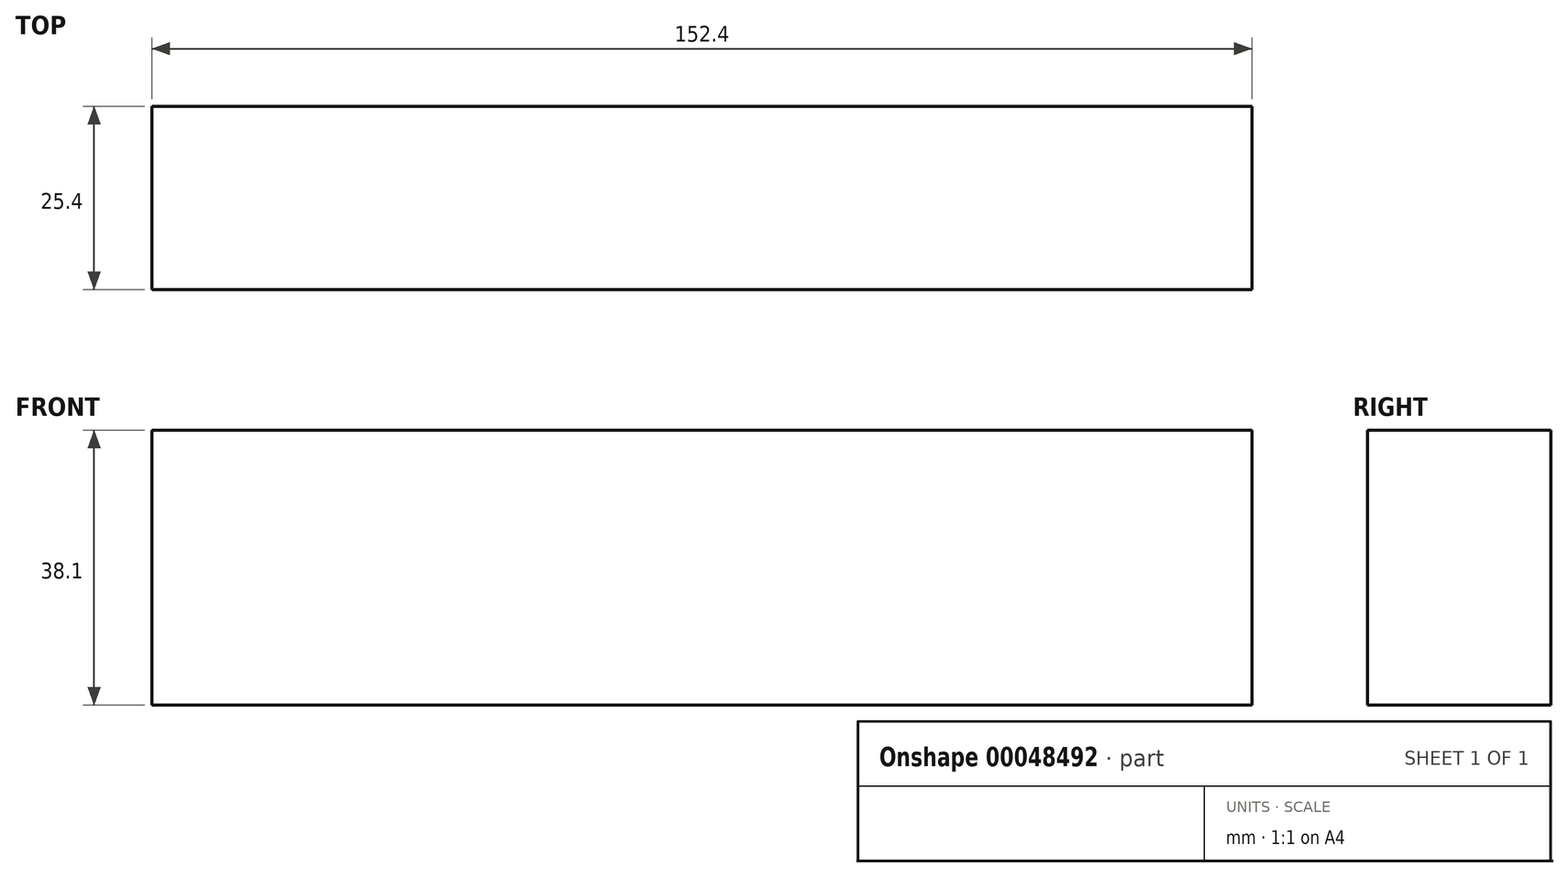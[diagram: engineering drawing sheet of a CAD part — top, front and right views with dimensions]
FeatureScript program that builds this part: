
annotation { "Feature Type Name" : "Feature", "Feature Type Description" : "" }
export const myFeature = defineFeature(function(context is Context, id is Id, definition is map)
    precondition{}
    {
        {
            var Q0;
            Q0=qCreatedBy(makeId("Front.planeOp"),FACE);
            var sketch = newSketch(context, id + "F0", { "sketchPlane" : qUnion([Q0])});
            skLineSegment(sketch, "E0", {"start": v(-76.2, 0) * mm, "end": v(76.2, 0) * mm});
            skLineSegment(sketch, "E1", {"start": v(-76.2, 0) * mm, "end": v(-76.2, 38.1) * mm});
            skLineSegment(sketch, "E2", {"start": v(-76.2, 38.1) * mm, "end": v(76.2, 38.1) * mm});
            skLineSegment(sketch, "E3", {"start": v(76.2, 38.1) * mm, "end": v(76.2, 0) * mm});
            skSolve(sketch);
        }
        {
            var Q0;
            Q0=makeQuery(id+"F0.imprint","IMPRINT",FACE,{"disambiguationData":[TD([[makeQuery(id+"F0.imprint","IMPRINT",EDGE,{"derivedFrom":sQuery(id+"F0.wireOp",EDGE,"E0")}),1.0]])]});
            extrude(context, id + "F1", {"entities" : qUnion([Q0]), "depth" : 25.4 * mm});
        }
    });
